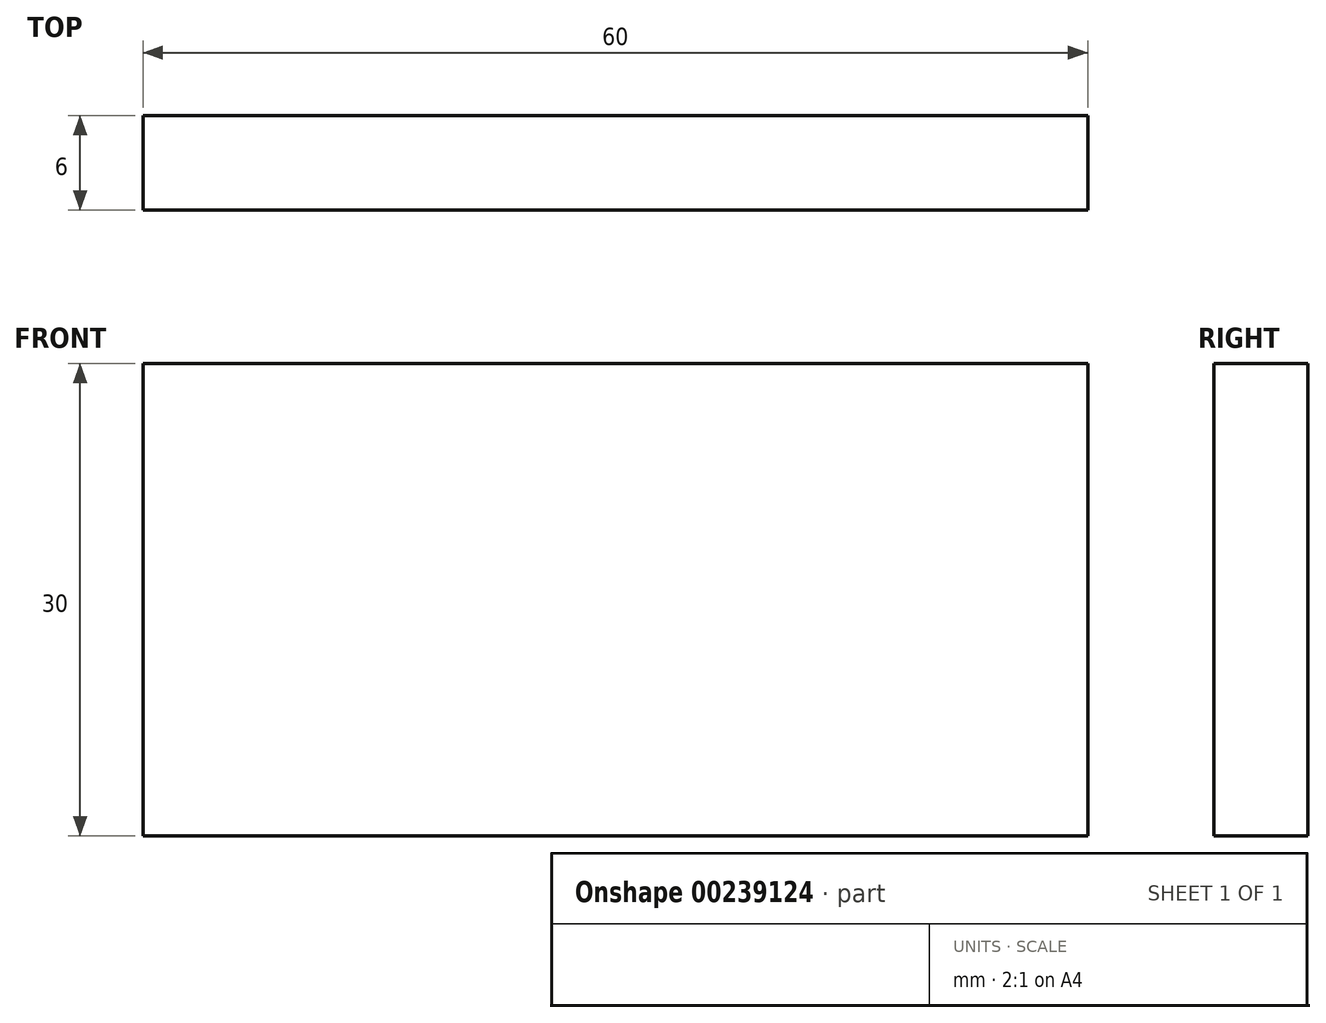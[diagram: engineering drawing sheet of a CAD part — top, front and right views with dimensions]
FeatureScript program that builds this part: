
annotation { "Feature Type Name" : "Feature", "Feature Type Description" : "" }
export const myFeature = defineFeature(function(context is Context, id is Id, definition is map)
    precondition{}
    {
        {
            assignVariable(context, id + "F0", {"name" : "v", "anyValue" : 3});
        }
        {
            var Q0;
            Q0=qCreatedBy(makeId("Front.planeOp"),FACE);
            var sketch = newSketch(context, id + "F1", { "sketchPlane" : qUnion([Q0])});
            skLineSegment(sketch, "E0.bottom", {"start": v(15, 15) * mm, "end": v(-15, 15) * mm});
            skLineSegment(sketch, "E0.top", {"start": v(15, -15) * mm, "end": v(-15, -15) * mm});
            skLineSegment(sketch, "E0.left", {"start": v(15, 15) * mm, "end": v(15, -15) * mm});
            skLineSegment(sketch, "E0.right", {"start": v(-15, 15) * mm, "end": v(-15, -15) * mm});
            skPoint(sketch, "E0.middle", {"position": v(0, 0) * mm});
            skSolve(sketch);
        }
        {
            var Q0;
            Q0=qSketchRegion(id+"F1",true);
            extrude(context, id + "F2", {"entities" : qUnion([Q0]), "endBound" : BoundingType.SYMMETRIC, "depth" : (2 * getVariable(context, 'v')) * mm});
        }
        {
            var Q0;
            Q0=makeQuery(id+"F2.opExtrude","CAP_FACE",FACE,{"disambiguationData":[OSD([sQuery(id+"F1.wireOp",EDGE,"E0.bottom"),sQuery(id+"F1.wireOp",EDGE,"E0.top"),sQuery(id+"F1.wireOp",EDGE,"E0.left"),sQuery(id+"F1.wireOp",EDGE,"E0.right")])],"isStart":false});
            var sketch = newSketch(context, id + "F3", { "sketchPlane" : qUnion([Q0])});
            skLineSegment(sketch, "E1.bottom", {"start": v(15, 15) * mm, "end": v(45, 15) * mm});
            skLineSegment(sketch, "E1.top", {"start": v(15, -15) * mm, "end": v(45, -15) * mm});
            skLineSegment(sketch, "E1.left", {"start": v(15, 15) * mm, "end": v(15, -15) * mm});
            skLineSegment(sketch, "E1.right", {"start": v(45, 15) * mm, "end": v(45, -15) * mm});
            skSolve(sketch);
        }
        {
            var Q0;
            Q0 = qSketchRegion(id + "F3", true);
            extrude(context, id + "F4", {"entities" : qUnion([Q0]), "operationType" : NewBodyOperationType.ADD, "oppositeDirection" : true, "depth" : (2 * getVariable(context, 'v')) * mm});
        }
    });
